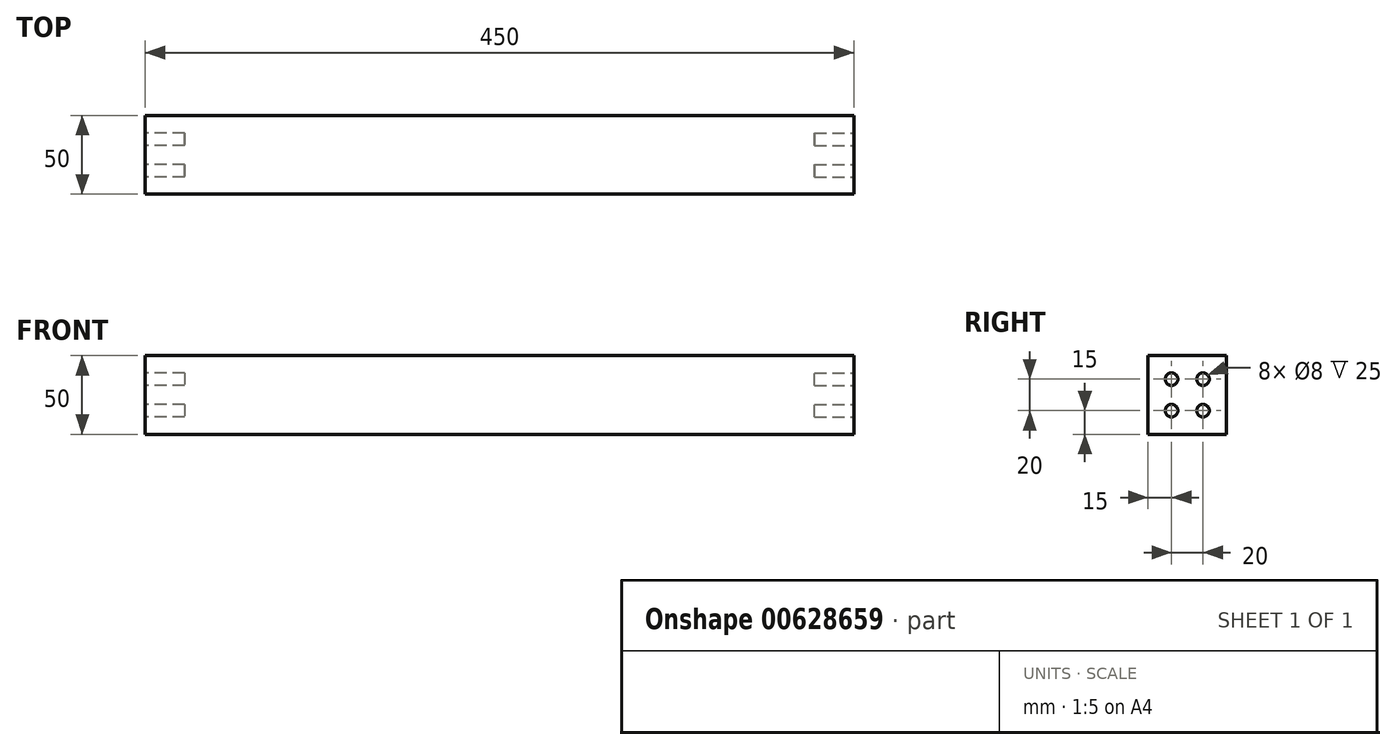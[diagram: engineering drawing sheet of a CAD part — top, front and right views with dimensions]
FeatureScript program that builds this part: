
annotation { "Feature Type Name" : "Feature", "Feature Type Description" : "" }
export const myFeature = defineFeature(function(context is Context, id is Id, definition is map)
    precondition{}
    {
        {
            var Q0;
            Q0=qCreatedBy(makeId("Right.planeOp"),FACE);
            var sketch = newSketch(context, id + "F0", { "sketchPlane" : qUnion([Q0])});
            skLineSegment(sketch, "E0.bottom", {"start": v(-25, 25) * mm, "end": v(25, 25) * mm});
            skLineSegment(sketch, "E0.top", {"start": v(-25, -25) * mm, "end": v(25, -25) * mm});
            skLineSegment(sketch, "E0.left", {"start": v(-25, 25) * mm, "end": v(-25, -25) * mm});
            skLineSegment(sketch, "E0.right", {"start": v(25, 25) * mm, "end": v(25, -25) * mm});
            skPoint(sketch, "E0.middle", {"position": v(0, 0) * mm});
            skSolve(sketch);
        }
        {
            var Q0;
            Q0=makeQuery(id+"F0.imprint","IMPRINT",FACE,{"disambiguationData":[TD([[makeQuery(id+"F0.imprint","IMPRINT",EDGE,{"derivedFrom":sQuery(id+"F0.wireOp",EDGE,"E0.bottom")}),-1.0]])]});
            extrude(context, id + "F1", {"entities" : qUnion([Q0]), "endBound" : BoundingType.SYMMETRIC, "depth" : 450 * mm, "offsetDistance" : 25 * mm});
        }
        {
            var Q0;
            Q0=makeQuery(id+"F1.opExtrude","CAP_FACE",FACE,{"disambiguationData":[OSD([sQuery(id+"F0.wireOp",EDGE,"E0.bottom"),sQuery(id+"F0.wireOp",EDGE,"E0.top"),sQuery(id+"F0.wireOp",EDGE,"E0.left"),sQuery(id+"F0.wireOp",EDGE,"E0.right")])],"isStart":false});
            var sketch = newSketch(context, id + "F2", { "sketchPlane" : qUnion([Q0])});
            skCircle(sketch, "E1", {"center": v(-10, 10) * mm, "radius": 4 * mm});
            skCircle(sketch, "E2", {"center": v(10, 10) * mm, "radius": 4 * mm});
            skCircle(sketch, "E3", {"center": v(-10, -10) * mm, "radius": 4 * mm});
            skCircle(sketch, "E4", {"center": v(10, -10) * mm, "radius": 4 * mm});
            skSolve(sketch);
        }
        {
            var Q0;
            Q0=makeQuery(id+"F2.imprint","IMPRINT",FACE,{"disambiguationData":[TD([[makeQuery(id+"F2.imprint","IMPRINT",EDGE,{"derivedFrom":sQuery(id+"F2.wireOp",EDGE,"E1")}),1.0]])]});
            var Q1;
            Q1=makeQuery(id+"F2.imprint","IMPRINT",FACE,{"disambiguationData":[TD([[makeQuery(id+"F2.imprint","IMPRINT",EDGE,{"derivedFrom":sQuery(id+"F2.wireOp",EDGE,"E2")}),1.0]])]});
            var Q2;
            Q2=makeQuery(id+"F2.imprint","IMPRINT",FACE,{"disambiguationData":[TD([[makeQuery(id+"F2.imprint","IMPRINT",EDGE,{"derivedFrom":sQuery(id+"F2.wireOp",EDGE,"E4")}),1.0]])]});
            var Q3;
            Q3=makeQuery(id+"F2.imprint","IMPRINT",FACE,{"disambiguationData":[TD([[makeQuery(id+"F2.imprint","IMPRINT",EDGE,{"derivedFrom":sQuery(id+"F2.wireOp",EDGE,"E3")}),1.0]])]});
            extrude(context, id + "F3", {"entities" : qUnion([Q0, Q1, Q2, Q3]), "operationType" : NewBodyOperationType.REMOVE, "oppositeDirection" : true, "depth" : 25 * mm, "offsetDistance" : 25 * mm});
        }
        {
            var Q0;
            Q0=makeQuery(id+"F1.opExtrude","CAP_FACE",FACE,{"disambiguationData":[OSD([sQuery(id+"F0.wireOp",EDGE,"E0.bottom"),sQuery(id+"F0.wireOp",EDGE,"E0.top"),sQuery(id+"F0.wireOp",EDGE,"E0.left"),sQuery(id+"F0.wireOp",EDGE,"E0.right")])],"isStart":true});
            var sketch = newSketch(context, id + "F4", { "sketchPlane" : qUnion([Q0])});
            skCircle(sketch, "E5", {"center": v(-10, 10) * mm, "radius": 4 * mm});
            skCircle(sketch, "E6", {"center": v(10, 10) * mm, "radius": 4 * mm});
            skCircle(sketch, "E7", {"center": v(-10, -10) * mm, "radius": 4 * mm});
            skCircle(sketch, "E8", {"center": v(10, -10) * mm, "radius": 4 * mm});
            skSolve(sketch);
        }
        {
            var Q0;
            Q0=makeQuery(id+"F4.imprint","IMPRINT",FACE,{"disambiguationData":[TD([[makeQuery(id+"F4.imprint","IMPRINT",EDGE,{"derivedFrom":sQuery(id+"F4.wireOp",EDGE,"E5")}),1.0]])]});
            var Q1;
            Q1=makeQuery(id+"F4.imprint","IMPRINT",FACE,{"disambiguationData":[TD([[makeQuery(id+"F4.imprint","IMPRINT",EDGE,{"derivedFrom":sQuery(id+"F4.wireOp",EDGE,"E6")}),1.0]])]});
            var Q2;
            Q2=makeQuery(id+"F4.imprint","IMPRINT",FACE,{"disambiguationData":[TD([[makeQuery(id+"F4.imprint","IMPRINT",EDGE,{"derivedFrom":sQuery(id+"F4.wireOp",EDGE,"E8")}),1.0]])]});
            var Q3;
            Q3=makeQuery(id+"F4.imprint","IMPRINT",FACE,{"disambiguationData":[TD([[makeQuery(id+"F4.imprint","IMPRINT",EDGE,{"derivedFrom":sQuery(id+"F4.wireOp",EDGE,"E7")}),1.0]])]});
            extrude(context, id + "F5", {"entities" : qUnion([Q0, Q1, Q2, Q3]), "operationType" : NewBodyOperationType.REMOVE, "oppositeDirection" : true, "depth" : 25 * mm, "offsetDistance" : 25 * mm});
        }
    });
